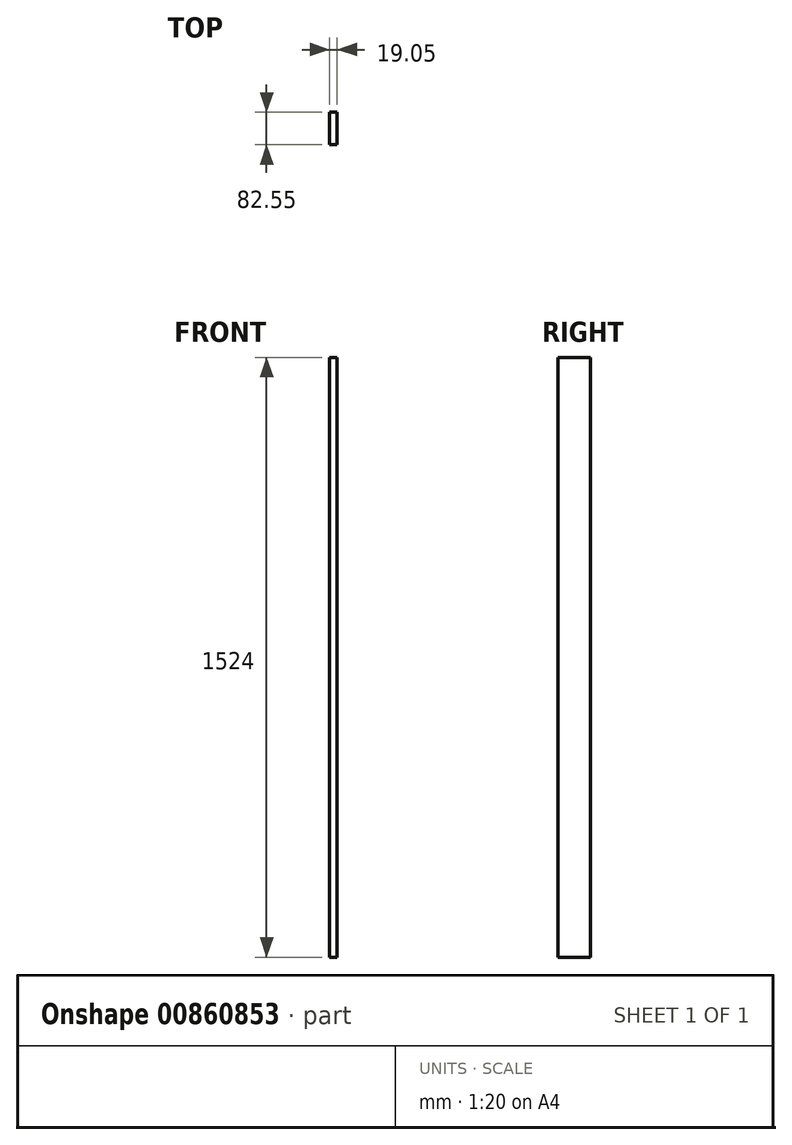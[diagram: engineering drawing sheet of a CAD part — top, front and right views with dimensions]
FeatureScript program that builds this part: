
annotation { "Feature Type Name" : "Feature", "Feature Type Description" : "" }
export const myFeature = defineFeature(function(context is Context, id is Id, definition is map)
    precondition{}
    {
        {
            var Q0;
            Q0=qCreatedBy(makeId("Front.planeOp"),FACE);
            var sketch = newSketch(context, id + "F0", { "sketchPlane" : qUnion([Q0])});
            skLineSegment(sketch, "E0.bottom", {"start": v(-130.08, 767.55) * mm, "end": v(-111.03, 767.55) * mm});
            skLineSegment(sketch, "E0.top", {"start": v(-130.08, -756.45) * mm, "end": v(-111.03, -756.45) * mm});
            skLineSegment(sketch, "E0.left", {"start": v(-130.08, 767.55) * mm, "end": v(-130.08, -756.45) * mm});
            skLineSegment(sketch, "E0.right", {"start": v(-111.03, 767.55) * mm, "end": v(-111.03, -756.45) * mm});
            skSolve(sketch);
        }
        {
            var Q0;
            Q0 = qSketchRegion(id + "F0", true);
            extrude(context, id + "F1", {"entities" : qUnion([Q0]), "depth" : 82.55 * mm, "offsetDistance" : 25.4 * mm});
        }
    });
